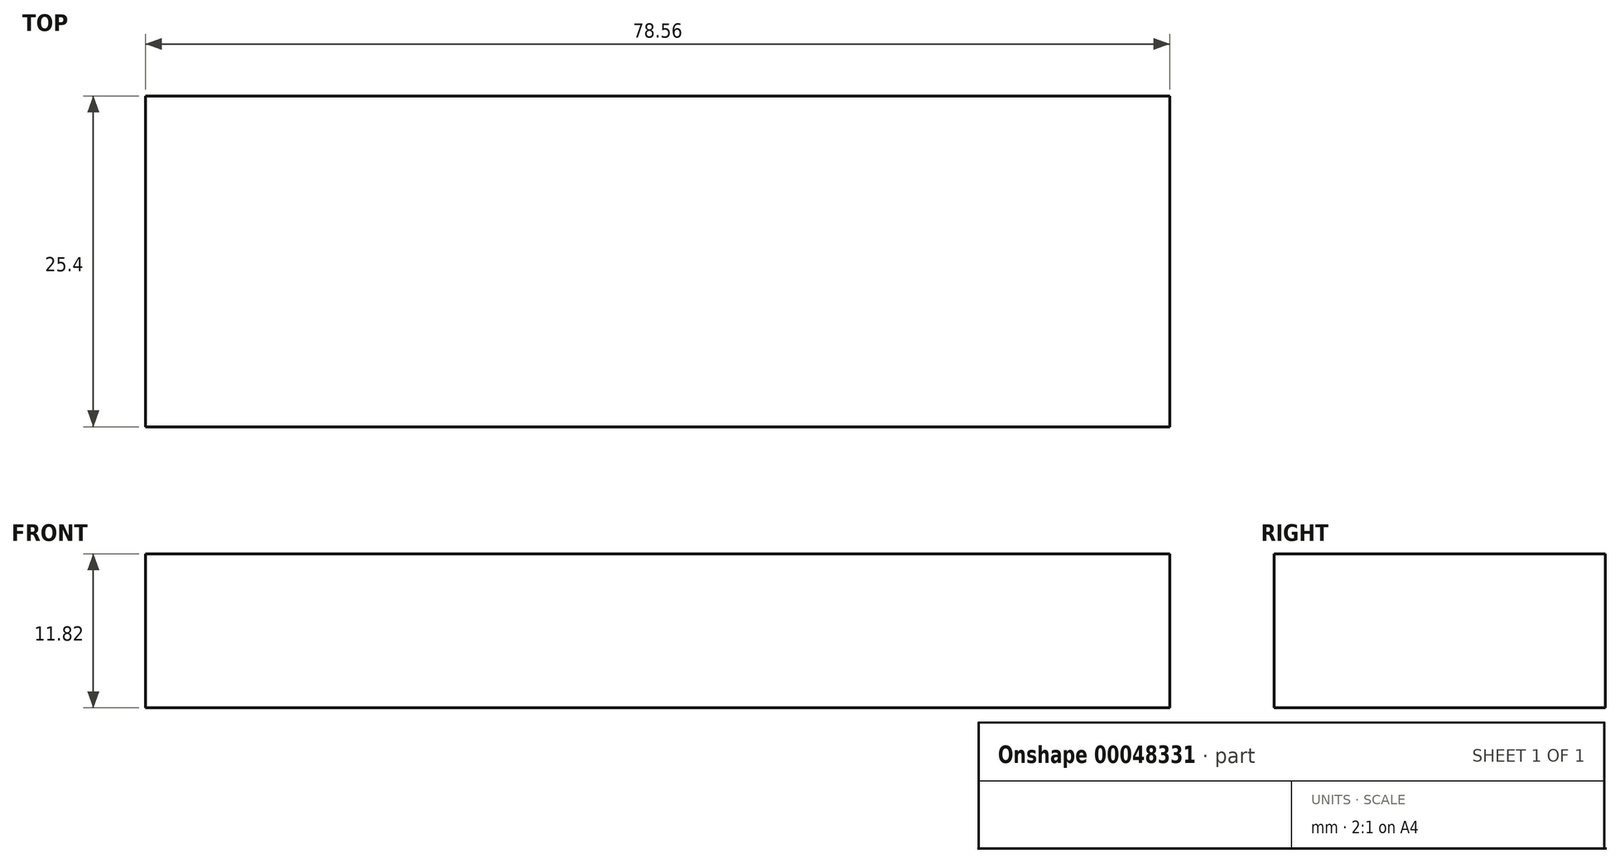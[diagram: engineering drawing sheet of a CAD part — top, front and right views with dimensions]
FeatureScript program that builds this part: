
annotation { "Feature Type Name" : "Feature", "Feature Type Description" : "" }
export const myFeature = defineFeature(function(context is Context, id is Id, definition is map)
    precondition{}
    {
        {
            var Q0;
            Q0=qCreatedBy(makeId("Front.planeOp"),FACE);
            var sketch = newSketch(context, id + "F0", { "sketchPlane" : qUnion([Q0])});
            skLineSegment(sketch, "E0.rect.bottom", {"start": v(-31.3, -4.1) * mm, "end": v(-109.86, -4.1) * mm});
            skLineSegment(sketch, "E0.rect.top", {"start": v(-31.3, -15.92) * mm, "end": v(-109.86, -15.92) * mm});
            skLineSegment(sketch, "E0.rect.left", {"start": v(-31.3, -4.1) * mm, "end": v(-31.3, -15.92) * mm});
            skLineSegment(sketch, "E0.rect.right", {"start": v(-109.86, -4.1) * mm, "end": v(-109.86, -15.92) * mm});
            skPoint(sketch, "E0.rect.middle", {"position": v(-70.58, -10.01) * mm});
            skSolve(sketch);
        }
        {
            var Q0;
            Q0=makeQuery(id+"F0.imprint","IMPRINT",FACE,{"disambiguationData":[TD([[makeQuery(id+"F0.imprint","IMPRINT",EDGE,{"derivedFrom":sQuery(id+"F0.wireOp",EDGE,"E0.rect.bottom")}),1.0]])]});
            extrude(context, id + "F1", {"entities" : qUnion([Q0]), "depth" : 25.4 * mm});
        }
    });
